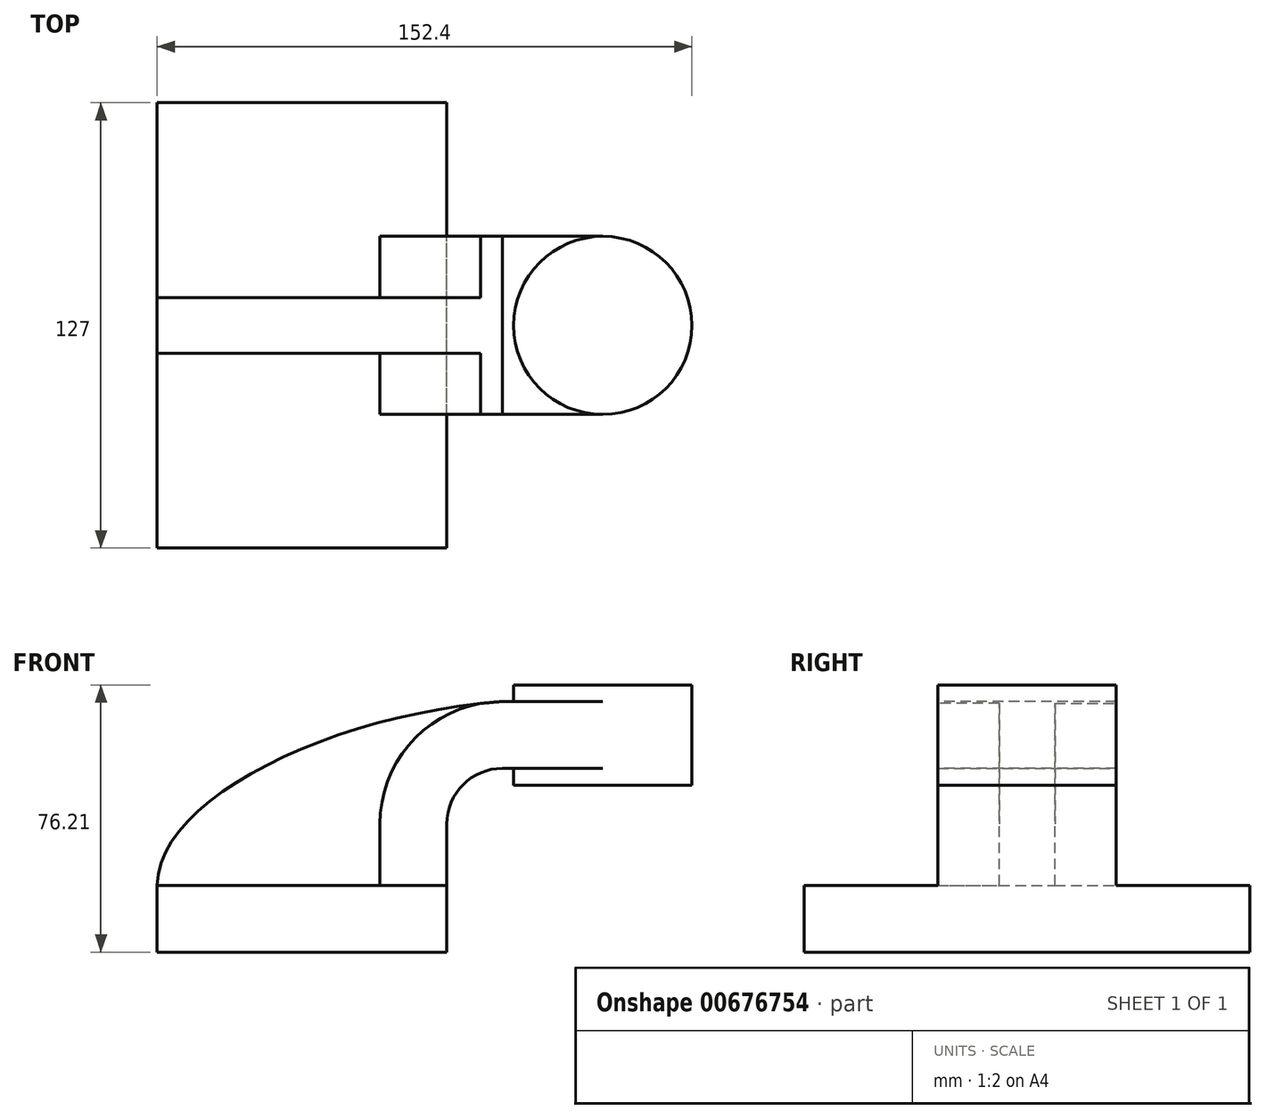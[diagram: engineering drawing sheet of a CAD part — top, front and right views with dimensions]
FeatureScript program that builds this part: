
annotation { "Feature Type Name" : "Feature", "Feature Type Description" : "" }
export const myFeature = defineFeature(function(context is Context, id is Id, definition is map)
    precondition{}
    {
        {
            var Q0;
            Q0=qCreatedBy(makeId("Front.planeOp"),FACE);
            var sketch = newSketch(context, id + "F0", { "sketchPlane" : qUnion([Q0])});
            skLineSegment(sketch, "E0.bottom", {"start": v(-7.95, -9.53) * mm, "end": v(-90.5, -9.52) * mm});
            skLineSegment(sketch, "E0.top", {"start": v(-7.95, 9.53) * mm, "end": v(-90.5, 9.53) * mm});
            skLineSegment(sketch, "E0.left", {"start": v(-7.95, -9.53) * mm, "end": v(-7.95, 9.53) * mm});
            skLineSegment(sketch, "E0.right", {"start": v(-90.5, -9.52) * mm, "end": v(-90.5, 9.53) * mm});
            skPoint(sketch, "E0.middle", {"position": v(-49.23, 0) * mm});
            skLineSegment(sketch, "E1.bottom", {"start": v(11.1, 38.1) * mm, "end": v(61.9, 38.1) * mm});
            skLineSegment(sketch, "E1.top", {"start": v(11.1, 66.67) * mm, "end": v(61.9, 66.67) * mm});
            skLineSegment(sketch, "E1.left", {"start": v(11.1, 38.1) * mm, "end": v(11.1, 66.67) * mm});
            skLineSegment(sketch, "E1.right", {"start": v(61.9, 38.1) * mm, "end": v(61.9, 66.67) * mm});
            skPoint(sketch, "E1.middle", {"position": v(36.5, 52.39) * mm});
            skLineSegment(sketch, "E2", {"start": v(-7.95, 9.53) * mm, "end": v(-7.95, 27) * mm});
            skArc(sketch, "E3", {"start": v(-7.95, 27) * mm, "mid": v(-3.3, 38.23) * mm, "end": v(7.92, 42.88) * mm});
            skPoint(sketch, "E4.orphan", {"position": v(0, 45.9) * mm});
            skLineSegment(sketch, "E5", {"start": v(7.92, 42.88) * mm, "end": v(11.1, 42.88) * mm});
            skLineSegment(sketch, "E6", {"start": v(11.1, 42.88) * mm, "end": v(36.5, 42.88) * mm});
            skLineSegment(sketch, "E7.0", {"start": v(7.92, 61.93) * mm, "end": v(11.1, 61.93) * mm});
            skArc(sketch, "E7.1", {"start": v(-27, 27) * mm, "mid": v(-16.77, 51.7) * mm, "end": v(7.92, 61.93) * mm});
            skLineSegment(sketch, "E7.2", {"start": v(-27, 9.53) * mm, "end": v(-27, 27) * mm});
            skLineSegment(sketch, "E8", {"start": v(11.1, 61.93) * mm, "end": v(36.5, 61.93) * mm});
            skLineSegment(sketch, "E9", {"start": v(36.5, 66.67) * mm, "end": v(36.5, 38.1) * mm});
            skFitSpline(sketch, "E10", {"points": [v(-90.5, 9.53) * mm, v(7.92, 61.93) * mm], "startDerivative": vector(0.88, 75.55) * mm, "endDerivative": vector(143.3, 10.35) * mm});
            skSolve(sketch);
        }
        {
            var Q0;
            Q0=makeQuery(id+"F0.imprint","IMPRINT",FACE,{"disambiguationData":[TD([[makeQuery(id+"F0.imprint","IMPRINT",EDGE,{"derivedFrom":sQuery(id+"F0.wireOp",EDGE,"E0.bottom")}),-1.0]])]});
            extrude(context, id + "F1", {"entities" : qUnion([Q0]), "endBound" : BoundingType.SYMMETRIC, "depth" : 127 * mm, "offsetDistance" : 25.4 * mm});
        }
        {
            var Q0;
            {var subQ0=sQuery(id+"F0.wireOp",EDGE,"E2");Q0=makeQuery(id+"F0.imprint","IMPRINT",FACE,{"disambiguationData":[TD([[makeQuery(id+"F0.imprint","IMPRINT",EDGE,{"derivedFrom":subQ0}),1.0]])]});}
            var Q1;
            {var subQ0=sQuery(id+"F0.wireOp",EDGE,"E6");Q1=makeQuery(id+"F0.imprint","IMPRINT",FACE,{"disambiguationData":[TD([[makeQuery(id+"F0.imprint","IMPRINT",EDGE,{"derivedFrom":subQ0}),1.0]])]});}
            extrude(context, id + "F2", {"entities" : qUnion([Q0, Q1]), "operationType" : NewBodyOperationType.ADD, "endBound" : BoundingType.SYMMETRIC, "depth" : 50.8 * mm, "offsetDistance" : 25.4 * mm});
        }
        {
            var Q0;
            {var subQ3=sQuery(id+"F0.wireOp",EDGE,"E7.2");Q0=makeQuery(id+"F0.imprint","IMPRINT",FACE,{"disambiguationData":[TD([[makeQuery(id+"F0.imprint","IMPRINT",EDGE,{"derivedFrom":subQ3}),1.0]])]});}
            extrude(context, id + "F3", {"entities" : qUnion([Q0]), "operationType" : NewBodyOperationType.ADD, "endBound" : BoundingType.SYMMETRIC, "depth" : 15.88 * mm, "offsetDistance" : 25.4 * mm});
        }
        {
            var Q0;
            {var subQ4=sQuery(id+"F0.wireOp",EDGE,"E1.right");Q0=makeQuery(id+"F0.imprint","IMPRINT",FACE,{"disambiguationData":[TD([[makeQuery(id+"F0.imprint","IMPRINT",EDGE,{"derivedFrom":subQ4}),1.0]])]});}
            var Q1;
            Q1=sQuery(id+"F0.wireOp",EDGE,"E9");
            revolve(context, id + "F4", {"operationType" : NewBodyOperationType.ADD, "entities" : qUnion([Q0]), "axis" : qUnion([Q1]), "revolveType" : RevolveType.FULL});
        }
    });
